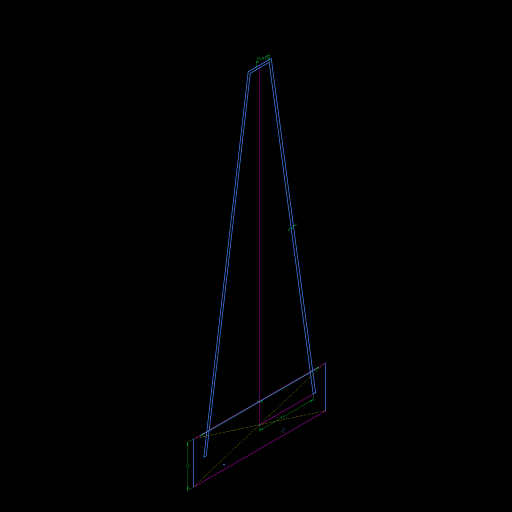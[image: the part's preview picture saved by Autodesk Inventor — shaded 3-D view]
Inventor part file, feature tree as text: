
AUTODESK INVENTOR PART (.ipt)
format: ipt  version: 2023 (Build 270158000, 158)  size: 83,456 bytes
history: native  units: mm
features: sketch x1
ambient origin geometry x8: Origin, YZ Plane, XZ Plane, XY Plane, X Axis, Y Axis, Z Axis, Center Point
feature tree (1):
  sketch  "Sketch1"  dims[d0=100.0mm d4=10.93871mm d5=2.0mm d6=45.0mm d7=35.0mm]
